# Revit family: Casement_36_F_Side_Hung_Standard
name_source: partatom
category: Windows
revit_build: Autodesk Revit 2014 (Build: 20130308_1515(x64)
units: mm (PartAtom-declared; Revit-internal decimal feet)

## types (12) — shared parameters
Aluminium Thickness = 1 mm  [stored 0.00328084 ft]
Area Pane Left Top = 0.52 m²
Area Pane Right Top = 0.52 m²
Bead SG Gap = 13 mm  [stored 0.0426509 ft]
Casement Dimension = 36 mm  [stored 0.11811 ft]
Custom Sash Left Height = 1154 mm  [stored 3.78609 ft]
Custom Sash Left Width = 554 mm  [stored 1.81759 ft]
Custom Sash Right Height = 1154 mm  [stored 3.78609 ft]
Custom Sash Right Width = 554 mm  [stored 1.81759 ft]
DG Extrusion Start = 8 mm  [stored 0.0262467 ft]
DG Gasket Finish = Double Glazing Gasket Material
DG Thickness Calc = 4 mm  [stored 0.0131234 ft]
Default Sill Height = 800 mm  [stored 2.62467 ft]
Depth Bead = 22 mm  [stored 0.0721785 ft]
Description = Window 36mm, Type F side hung
Frame Center Offset = 18 mm  [stored 0.0590551 ft]
Height Sash Left = 1124 mm
Height Sash Left Opening = 1154 mm  [stored 3.78609 ft]
Height Sash Right = 1124 mm
Height Sash Right Opening = 1154 mm  [stored 3.78609 ft]
Length Transom Left = 540 mm  [stored 1.77165 ft]
Length Transom Right = 540 mm  [stored 1.77165 ft]
Limit Fixed Pane Height Max = 1800 mm
Limit Fixed Pane Height Min = 200 mm  [stored 0.656168 ft]
Limit Fixed Pane Width Max = 1500 mm  [stored 4.92126 ft]
Limit Fixed Pane Width Min = 200 mm  [stored 0.656168 ft]
Limit Sash Height Max = 1300 mm  [stored 4.26509 ft]
Limit Sash Height Min = 300 mm  [stored 0.984252 ft]
Limit Sash Width Max = 600 mm  [stored 1.9685 ft]
Limit Sash Width Min = 300 mm  [stored 0.984252 ft]
Limit Window Height Max = 1860 mm
Limit Window Height Min = 1430 mm  [stored 4.6916 ft]
Limit Window Width Max = 2700 mm
Limit Window Width Min = 1400 mm
Manufacturer = Crealco
Max System DG One Piece Thickness = 6 mm  [stored 0.019685 ft]
Max System DG Unit Thickness = 25 mm  [stored 0.082021 ft]
Model = Casement 36
Offset Bead Center Reversed = 18 mm  [stored 0.0590551 ft]
Offset Fixed Panel Center Left = 600 mm  [stored 1.9685 ft]
Offset Mullion Left = 570 mm  [stored 1.87008 ft]
Offset Mullion Right = 570 mm  [stored 1.87008 ft]
Offset Sash Side = 23 mm  [stored 0.0754593 ft]
Offset Sash Top = 23 mm  [stored 0.0754593 ft]
Offset Transom Left Top = 1170 mm
Offset Transom Right Top = 1170 mm
Offset Window Exterior = 18 mm  [stored 0.0590551 ft]
SG Gasket Thickness = 6 mm  [stored 0.019685 ft]
Sash Center Offset = 15 mm  [stored 0.0492126 ft]
Sash Overlap = 7 mm  [stored 0.0229659 ft]
Sash Spacing Inner = 8 mm  [stored 0.0262467 ft]
Side Hung Left = Yes
Side Hung Right = No
URL = http://www.crealco.co.za
Wall Closure = By host
Width Bead = 15 mm  [stored 0.0492126 ft]
Width Fixed Panel Left = 540 mm  [stored 1.77165 ft]
Width Fixed Panel Right = 540 mm  [stored 1.77165 ft]
Width Profile = 30 mm  [stored 0.0984252 ft]
Width Sash Left = 524 mm  [stored 1.71916 ft]
Width Sash Left Opening = 554 mm  [stored 1.81759 ft]
Width Sash Right = 524 mm  [stored 1.71916 ft]
Width Sash Right Opening = 554 mm  [stored 1.81759 ft]
zero-valued in all types: Window Exterior Offset

## per-type parameters (varying)
- 36-1815SS-1000Pa: Area Pane Left Bottom=0.13 m²; Area Pane Middle=0.82 m²; Area Pane Right Bottom=0.13 m²; Clearvue Insulated LowE SHGC Value=0.536; Clearvue Insulated LowE U Value=3.8; Clearvue Insulated SHGC Value=0.589; Clearvue Insulated U Value=4.37; Clearvue SHGC Value=0.669; Clearvue U Value=6.69; Corrected Mullion Size=0 mm  [stored 0 ft]; Custom Windload=1000 mm  [stored 3.28084 ft]; Custom Window Height=1490 mm  [stored 4.88845 ft]; Custom Window Width=1790 mm  [stored 5.8727 ft]; Depth Mullion=54 mm  [stored 0.177165 ft]; Energy Advantage SHGC Value=0.599; Energy Advantage U Value=5.1; Height=1490 mm  [stored 4.88845 ft]; Height Fixed Panel Center=1430 mm  [stored 4.6916 ft]; Height Fixed Panel Left=260 mm; Height Fixed Panel Right=260 mm; Intruderprufe Insulated LowE SHGC Value=0.495; Intruderprufe Insulated LowE U Value=3.72; Intruderprufe Insulated SHGC Value=0.54; Intruderprufe Insulated U Value=4.26; Intruderprufe LowE SHGC Value=0.561; Intruderprufe LowE U Value=4.99; Intruderprufe SHGC Value=0.637; Intruderprufe U Value=6.54; Length Mullion=1490 mm  [stored 4.88845 ft]; Max Pane Area=0.82 m²; Mullion Depth Windload Based=54 mm  [stored 0.177165 ft]; Standard Mullion Different=0 mm  [stored 0 ft]; Width=1790 mm  [stored 5.8727 ft]; Width Fixed Panel Center=590 mm  [stored 1.9357 ft]; Windload Design=1000 mm  [stored 3.28084 ft]
- 36-2415SS-1000Pa: Area Pane Left Bottom=0.13 m²; Area Pane Middle=1.68 m²; Area Pane Right Bottom=0.13 m²; Clearvue Insulated LowE SHGC Value=0.594; Clearvue Insulated LowE U Value=3.59; Clearvue Insulated SHGC Value=0.653; Clearvue Insulated U Value=4.24; Clearvue SHGC Value=0; Clearvue U Value=7.9; Corrected Mullion Size=0 mm  [stored 0 ft]; Custom Windload=1000 mm  [stored 3.28084 ft]; Custom Window Height=1490 mm  [stored 4.88845 ft]; Custom Window Width=2390 mm; Depth Mullion=54 mm  [stored 0.177165 ft]; Energy Advantage SHGC Value=0; Energy Advantage U Value=7.9; Height=1490 mm  [stored 4.88845 ft]; Height Fixed Panel Center=1430 mm  [stored 4.6916 ft]; Height Fixed Panel Left=260 mm; Height Fixed Panel Right=260 mm; Intruderprufe Insulated LowE SHGC Value=0.548; Intruderprufe Insulated LowE U Value=3.51; Intruderprufe Insulated SHGC Value=0.6; Intruderprufe Insulated U Value=4.14; Intruderprufe LowE SHGC Value=0.62; Intruderprufe LowE U Value=4.95; Intruderprufe SHGC Value=0.705; Intruderprufe U Value=6.7; Length Mullion=1490 mm  [stored 4.88845 ft]; Max Pane Area=1.68 m²; Mullion Depth Windload Based=54 mm  [stored 0.177165 ft]; Standard Mullion Different=0 mm  [stored 0 ft]; Width=2390 mm; Width Fixed Panel Center=1190 mm; Windload Design=1000 mm  [stored 3.28084 ft]
- 36-1818SS-1000Pa: Area Pane Left Bottom=0.29 m²; Area Pane Middle=1 m²; Area Pane Right Bottom=0.29 m²; Clearvue Insulated LowE SHGC Value=0.577; Clearvue Insulated LowE U Value=3.87; Clearvue Insulated SHGC Value=0.634; Clearvue Insulated U Value=4.49; Clearvue SHGC Value=0.721; Clearvue U Value=7.01; Corrected Mullion Size=54 mm  [stored 0.177165 ft]; Custom Windload=1000 mm  [stored 3.28084 ft]; Custom Window Height=1790 mm  [stored 5.8727 ft]; Custom Window Width=1790 mm  [stored 5.8727 ft]; Depth Mullion=54 mm  [stored 0.177165 ft]; Energy Advantage SHGC Value=0.645; Energy Advantage U Value=5.28; Height=1790 mm  [stored 5.8727 ft]; Height Fixed Panel Center=1730 mm  [stored 5.67585 ft]; Height Fixed Panel Left=560 mm  [stored 1.83727 ft]; Height Fixed Panel Right=560 mm  [stored 1.83727 ft]; Intruderprufe Insulated LowE SHGC Value=0.533; Intruderprufe Insulated LowE U Value=3.79; Intruderprufe Insulated SHGC Value=0.582; Intruderprufe Insulated U Value=4.38; Intruderprufe LowE SHGC Value=0.603; Intruderprufe LowE U Value=5.16; Intruderprufe SHGC Value=0.686; Intruderprufe U Value=6.85; Length Mullion=1790 mm  [stored 5.8727 ft]; Max Pane Area=1 m²; Mullion Depth Windload Based=54 mm  [stored 0.177165 ft]; Standard Mullion Different=1 mm  [stored 0.00328084 ft]; Width=1790 mm  [stored 5.8727 ft]; Width Fixed Panel Center=590 mm  [stored 1.9357 ft]; Windload Design=1000 mm  [stored 3.28084 ft]
- 36-2418SS-1000Pa: Area Pane Left Bottom=0.29 m²; Area Pane Middle=2.03 m²; Area Pane Right Bottom=0.29 m²; Clearvue Insulated LowE SHGC Value=0.655; Clearvue Insulated LowE U Value=3.77; Clearvue Insulated SHGC Value=0.72; Clearvue Insulated U Value=4.49; Clearvue SHGC Value=0; Clearvue U Value=7.9; Corrected Mullion Size=0 mm  [stored 0 ft]; Custom Windload=1000 mm  [stored 3.28084 ft]; Custom Window Height=1790 mm  [stored 5.8727 ft]; Custom Window Width=2390 mm; Depth Mullion=70 mm  [stored 0.229659 ft]; Energy Advantage SHGC Value=0; Energy Advantage U Value=7.9; Height=1790 mm  [stored 5.8727 ft]; Height Fixed Panel Center=1730 mm  [stored 5.67585 ft]; Height Fixed Panel Left=560 mm  [stored 1.83727 ft]; Height Fixed Panel Right=560 mm  [stored 1.83727 ft]; Intruderprufe Insulated LowE SHGC Value=0.604; Intruderprufe Insulated LowE U Value=3.69; Intruderprufe Insulated SHGC Value=0.662; Intruderprufe Insulated U Value=4.38; Intruderprufe LowE SHGC Value=0.684; Intruderprufe LowE U Value=5.27; Intruderprufe SHGC Value=0.779; Intruderprufe U Value=7.22; Length Mullion=1790 mm  [stored 5.8727 ft]; Max Pane Area=2.03 m²; Mullion Depth Windload Based=70 mm  [stored 0.229659 ft]; Standard Mullion Different=0 mm  [stored 0 ft]; Width=2390 mm; Width Fixed Panel Center=1190 mm; Windload Design=1000 mm  [stored 3.28084 ft]
- 36-1815SS-1500Pa: Area Pane Left Bottom=0.13 m²; Area Pane Middle=0.82 m²; Area Pane Right Bottom=0.13 m²; Clearvue Insulated LowE SHGC Value=0.536; Clearvue Insulated LowE U Value=3.8; Clearvue Insulated SHGC Value=0.589; Clearvue Insulated U Value=4.37; Clearvue SHGC Value=0.669; Clearvue U Value=6.69; Corrected Mullion Size=0 mm  [stored 0 ft]; Custom Windload=1500 mm  [stored 4.92126 ft]; Custom Window Height=1490 mm  [stored 4.88845 ft]; Custom Window Width=1790 mm  [stored 5.8727 ft]; Depth Mullion=54 mm  [stored 0.177165 ft]; Energy Advantage SHGC Value=0.599; Energy Advantage U Value=5.1; Height=1490 mm  [stored 4.88845 ft]; Height Fixed Panel Center=1430 mm  [stored 4.6916 ft]; Height Fixed Panel Left=260 mm; Height Fixed Panel Right=260 mm; Intruderprufe Insulated LowE SHGC Value=0.495; Intruderprufe Insulated LowE U Value=3.72; Intruderprufe Insulated SHGC Value=0.54; Intruderprufe Insulated U Value=4.26; Intruderprufe LowE SHGC Value=0.561; Intruderprufe LowE U Value=4.99; Intruderprufe SHGC Value=0.637; Intruderprufe U Value=6.54; Length Mullion=1490 mm  [stored 4.88845 ft]; Max Pane Area=0.82 m²; Mullion Depth Windload Based=54 mm  [stored 0.177165 ft]; Standard Mullion Different=0 mm  [stored 0 ft]; Width=1790 mm  [stored 5.8727 ft]; Width Fixed Panel Center=590 mm  [stored 1.9357 ft]; Windload Design=1500 mm  [stored 4.92126 ft]
- 36-1815SS-2000Pa: Area Pane Left Bottom=0.13 m²; Area Pane Middle=0.82 m²; Area Pane Right Bottom=0.13 m²; Clearvue Insulated LowE SHGC Value=0.536; Clearvue Insulated LowE U Value=3.8; Clearvue Insulated SHGC Value=0.589; Clearvue Insulated U Value=4.37; Clearvue SHGC Value=0.669; Clearvue U Value=6.69; Corrected Mullion Size=0 mm  [stored 0 ft]; Custom Windload=2000 mm; Custom Window Height=1490 mm  [stored 4.88845 ft]; Custom Window Width=1790 mm  [stored 5.8727 ft]; Depth Mullion=70 mm  [stored 0.229659 ft]; Energy Advantage SHGC Value=0.599; Energy Advantage U Value=5.1; Height=1490 mm  [stored 4.88845 ft]; Height Fixed Panel Center=1430 mm  [stored 4.6916 ft]; Height Fixed Panel Left=260 mm; Height Fixed Panel Right=260 mm; Intruderprufe Insulated LowE SHGC Value=0.495; Intruderprufe Insulated LowE U Value=3.72; Intruderprufe Insulated SHGC Value=0.54; Intruderprufe Insulated U Value=4.26; Intruderprufe LowE SHGC Value=0.561; Intruderprufe LowE U Value=4.99; Intruderprufe SHGC Value=0.637; Intruderprufe U Value=6.54; Length Mullion=1490 mm  [stored 4.88845 ft]; Max Pane Area=0.82 m²; Mullion Depth Windload Based=70 mm  [stored 0.229659 ft]; Standard Mullion Different=0 mm  [stored 0 ft]; Width=1790 mm  [stored 5.8727 ft]; Width Fixed Panel Center=590 mm  [stored 1.9357 ft]; Windload Design=2000 mm
- 36-2415SS-1500Pa: Area Pane Left Bottom=0.13 m²; Area Pane Middle=1.68 m²; Area Pane Right Bottom=0.13 m²; Clearvue Insulated LowE SHGC Value=0.594; Clearvue Insulated LowE U Value=3.59; Clearvue Insulated SHGC Value=0.653; Clearvue Insulated U Value=4.24; Clearvue SHGC Value=0; Clearvue U Value=7.9; Corrected Mullion Size=0 mm  [stored 0 ft]; Custom Windload=1500 mm  [stored 4.92126 ft]; Custom Window Height=1490 mm  [stored 4.88845 ft]; Custom Window Width=2390 mm; Depth Mullion=54 mm  [stored 0.177165 ft]; Energy Advantage SHGC Value=0; Energy Advantage U Value=7.9; Height=1490 mm  [stored 4.88845 ft]; Height Fixed Panel Center=1430 mm  [stored 4.6916 ft]; Height Fixed Panel Left=260 mm; Height Fixed Panel Right=260 mm; Intruderprufe Insulated LowE SHGC Value=0.548; Intruderprufe Insulated LowE U Value=3.51; Intruderprufe Insulated SHGC Value=0.6; Intruderprufe Insulated U Value=4.14; Intruderprufe LowE SHGC Value=0.62; Intruderprufe LowE U Value=4.95; Intruderprufe SHGC Value=0.705; Intruderprufe U Value=6.7; Length Mullion=1490 mm  [stored 4.88845 ft]; Max Pane Area=1.68 m²; Mullion Depth Windload Based=54 mm  [stored 0.177165 ft]; Standard Mullion Different=0 mm  [stored 0 ft]; Width=2390 mm; Width Fixed Panel Center=1190 mm; Windload Design=1500 mm  [stored 4.92126 ft]
- 36-2415SS-2000Pa: Area Pane Left Bottom=0.13 m²; Area Pane Middle=1.68 m²; Area Pane Right Bottom=0.13 m²; Clearvue Insulated LowE SHGC Value=0.594; Clearvue Insulated LowE U Value=3.59; Clearvue Insulated SHGC Value=0.653; Clearvue Insulated U Value=4.24; Clearvue SHGC Value=0; Clearvue U Value=7.9; Corrected Mullion Size=0 mm  [stored 0 ft]; Custom Windload=2000 mm; Custom Window Height=1490 mm  [stored 4.88845 ft]; Custom Window Width=2390 mm; Depth Mullion=70 mm  [stored 0.229659 ft]; Energy Advantage SHGC Value=0; Energy Advantage U Value=7.9; Height=1490 mm  [stored 4.88845 ft]; Height Fixed Panel Center=1430 mm  [stored 4.6916 ft]; Height Fixed Panel Left=260 mm; Height Fixed Panel Right=260 mm; Intruderprufe Insulated LowE SHGC Value=0.548; Intruderprufe Insulated LowE U Value=3.51; Intruderprufe Insulated SHGC Value=0.6; Intruderprufe Insulated U Value=4.14; Intruderprufe LowE SHGC Value=0.62; Intruderprufe LowE U Value=4.95; Intruderprufe SHGC Value=0.705; Intruderprufe U Value=6.7; Length Mullion=1490 mm  [stored 4.88845 ft]; Max Pane Area=1.68 m²; Mullion Depth Windload Based=70 mm  [stored 0.229659 ft]; Standard Mullion Different=0 mm  [stored 0 ft]; Width=2390 mm; Width Fixed Panel Center=1190 mm; Windload Design=2000 mm
- 36-1818SS-1500Pa: Area Pane Left Bottom=0.29 m²; Area Pane Middle=1 m²; Area Pane Right Bottom=0.29 m²; Clearvue Insulated LowE SHGC Value=0.577; Clearvue Insulated LowE U Value=3.87; Clearvue Insulated SHGC Value=0.634; Clearvue Insulated U Value=4.49; Clearvue SHGC Value=0.721; Clearvue U Value=7.01; Corrected Mullion Size=0 mm  [stored 0 ft]; Custom Windload=1500 mm  [stored 4.92126 ft]; Custom Window Height=1790 mm  [stored 5.8727 ft]; Custom Window Width=1790 mm  [stored 5.8727 ft]; Depth Mullion=70 mm  [stored 0.229659 ft]; Energy Advantage SHGC Value=0.645; Energy Advantage U Value=5.28; Height=1790 mm  [stored 5.8727 ft]; Height Fixed Panel Center=1730 mm  [stored 5.67585 ft]; Height Fixed Panel Left=560 mm  [stored 1.83727 ft]; Height Fixed Panel Right=560 mm  [stored 1.83727 ft]; Intruderprufe Insulated LowE SHGC Value=0.533; Intruderprufe Insulated LowE U Value=3.79; Intruderprufe Insulated SHGC Value=0.582; Intruderprufe Insulated U Value=4.38; Intruderprufe LowE SHGC Value=0.603; Intruderprufe LowE U Value=5.16; Intruderprufe SHGC Value=0.686; Intruderprufe U Value=6.85; Length Mullion=1790 mm  [stored 5.8727 ft]; Max Pane Area=1 m²; Mullion Depth Windload Based=70 mm  [stored 0.229659 ft]; Standard Mullion Different=0 mm  [stored 0 ft]; Width=1790 mm  [stored 5.8727 ft]; Width Fixed Panel Center=590 mm  [stored 1.9357 ft]; Windload Design=1500 mm  [stored 4.92126 ft]
- 36-1818SS-2000Pa: Area Pane Left Bottom=0.29 m²; Area Pane Middle=1 m²; Area Pane Right Bottom=0.29 m²; Clearvue Insulated LowE SHGC Value=0.577; Clearvue Insulated LowE U Value=3.87; Clearvue Insulated SHGC Value=0.634; Clearvue Insulated U Value=4.49; Clearvue SHGC Value=0.721; Clearvue U Value=7.01; Corrected Mullion Size=70 mm  [stored 0.229659 ft]; Custom Windload=2000 mm; Custom Window Height=1790 mm  [stored 5.8727 ft]; Custom Window Width=1790 mm  [stored 5.8727 ft]; Depth Mullion=70 mm  [stored 0.229659 ft]; Energy Advantage SHGC Value=0.645; Energy Advantage U Value=5.28; Height=1790 mm  [stored 5.8727 ft]; Height Fixed Panel Center=1730 mm  [stored 5.67585 ft]; Height Fixed Panel Left=560 mm  [stored 1.83727 ft]; Height Fixed Panel Right=560 mm  [stored 1.83727 ft]; Intruderprufe Insulated LowE SHGC Value=0.533; Intruderprufe Insulated LowE U Value=3.79; Intruderprufe Insulated SHGC Value=0.582; Intruderprufe Insulated U Value=4.38; Intruderprufe LowE SHGC Value=0.603; Intruderprufe LowE U Value=5.16; Intruderprufe SHGC Value=0.686; Intruderprufe U Value=6.85; Length Mullion=1790 mm  [stored 5.8727 ft]; Max Pane Area=1 m²; Mullion Depth Windload Based=70 mm  [stored 0.229659 ft]; Standard Mullion Different=1 mm  [stored 0.00328084 ft]; Width=1790 mm  [stored 5.8727 ft]; Width Fixed Panel Center=590 mm  [stored 1.9357 ft]; Windload Design=2000 mm
- 36-2418SS-1500Pa: Area Pane Left Bottom=0.29 m²; Area Pane Middle=2.03 m²; Area Pane Right Bottom=0.29 m²; Clearvue Insulated LowE SHGC Value=0.655; Clearvue Insulated LowE U Value=3.77; Clearvue Insulated SHGC Value=0.72; Clearvue Insulated U Value=4.49; Clearvue SHGC Value=0; Clearvue U Value=7.9; Corrected Mullion Size=0 mm  [stored 0 ft]; Custom Windload=1500 mm  [stored 4.92126 ft]; Custom Window Height=1790 mm  [stored 5.8727 ft]; Custom Window Width=2390 mm; Depth Mullion=70 mm  [stored 0.229659 ft]; Energy Advantage SHGC Value=0; Energy Advantage U Value=7.9; Height=1790 mm  [stored 5.8727 ft]; Height Fixed Panel Center=1730 mm  [stored 5.67585 ft]; Height Fixed Panel Left=560 mm  [stored 1.83727 ft]; Height Fixed Panel Right=560 mm  [stored 1.83727 ft]; Intruderprufe Insulated LowE SHGC Value=0.604; Intruderprufe Insulated LowE U Value=3.69; Intruderprufe Insulated SHGC Value=0.662; Intruderprufe Insulated U Value=4.38; Intruderprufe LowE SHGC Value=0.684; Intruderprufe LowE U Value=5.27; Intruderprufe SHGC Value=0.779; Intruderprufe U Value=7.22; Length Mullion=1790 mm  [stored 5.8727 ft]; Max Pane Area=2.03 m²; Mullion Depth Windload Based=70 mm  [stored 0.229659 ft]; Standard Mullion Different=0 mm  [stored 0 ft]; Width=2390 mm; Width Fixed Panel Center=1190 mm; Windload Design=1500 mm  [stored 4.92126 ft]
- 36-2418SS-2000Pa: Area Pane Left Bottom=0.29 m²; Area Pane Middle=2.03 m²; Area Pane Right Bottom=0.29 m²; Clearvue Insulated LowE SHGC Value=0.656; Clearvue Insulated LowE U Value=3.8; Clearvue Insulated SHGC Value=0.721; Clearvue Insulated U Value=4.53; Clearvue SHGC Value=0; Clearvue U Value=7.9; Corrected Mullion Size=0 mm  [stored 0 ft]; Custom Windload=2000 mm; Custom Window Height=1790 mm  [stored 5.8727 ft]; Custom Window Width=2390 mm; Depth Mullion=90 mm  [stored 0.295276 ft]; Energy Advantage SHGC Value=0; Energy Advantage U Value=7.9; Height=1790 mm  [stored 5.8727 ft]; Height Fixed Panel Center=1730 mm  [stored 5.67585 ft]; Height Fixed Panel Left=560 mm  [stored 1.83727 ft]; Height Fixed Panel Right=560 mm  [stored 1.83727 ft]; Intruderprufe Insulated LowE SHGC Value=0.604; Intruderprufe Insulated LowE U Value=3.73; Intruderprufe Insulated SHGC Value=0.663; Intruderprufe Insulated U Value=4.42; Intruderprufe LowE SHGC Value=0.687; Intruderprufe LowE U Value=5.34; Intruderprufe SHGC Value=0.782; Intruderprufe U Value=7.29; Length Mullion=1790 mm  [stored 5.8727 ft]; Max Pane Area=2.03 m²; Mullion Depth Windload Based=90 mm  [stored 0.295276 ft]; Standard Mullion Different=0 mm  [stored 0 ft]; Width=2390 mm; Width Fixed Panel Center=1190 mm; Windload Design=2000 mm

note: [stored X ft] marks values corroborated as IEEE doubles in the binary element streams (Revit-internal decimal feet)

## geometry (parser evidence)
native form markers: Extrusion x1, Sweep x29
no freeform markers — native parametric forms only
